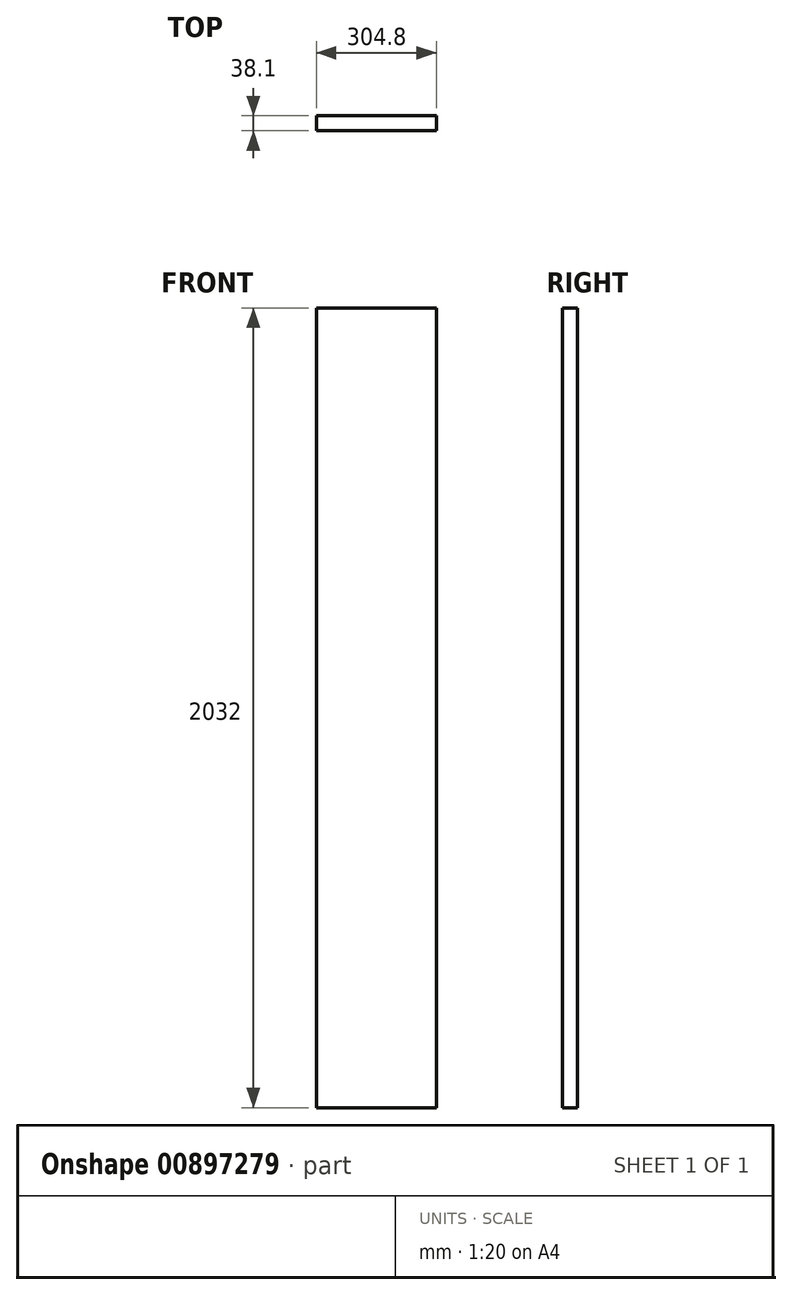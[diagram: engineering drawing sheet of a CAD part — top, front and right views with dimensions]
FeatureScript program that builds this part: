
annotation { "Feature Type Name" : "Feature", "Feature Type Description" : "" }
export const myFeature = defineFeature(function(context is Context, id is Id, definition is map)
    precondition{}
    {
        {
            var Q0;
            Q0=qCreatedBy(makeId("Front.planeOp"),FACE);
            var sketch = newSketch(context, id + "F0", { "sketchPlane" : qUnion([Q0])});
            skLineSegment(sketch, "E0.bottom", {"start": v(-152.4, 1016) * mm, "end": v(152.4, 1016) * mm});
            skLineSegment(sketch, "E0.top", {"start": v(-152.4, -1016) * mm, "end": v(152.4, -1016) * mm});
            skLineSegment(sketch, "E0.left", {"start": v(-152.4, 1016) * mm, "end": v(-152.4, -1016) * mm});
            skLineSegment(sketch, "E0.right", {"start": v(152.4, 1016) * mm, "end": v(152.4, -1016) * mm});
            skPoint(sketch, "E0.middle", {"position": v(0, 0) * mm});
            skSolve(sketch);
        }
        {
            var Q0;
            Q0=makeQuery(id+"F0.imprint","IMPRINT",FACE,{"disambiguationData":[TD([[makeQuery(id+"F0.imprint","IMPRINT",EDGE,{"derivedFrom":sQuery(id+"F0.wireOp",EDGE,"E0.bottom")}),-1.0]])]});
            extrude(context, id + "F1", {"entities" : qUnion([Q0]), "depth" : 38.1 * mm, "offsetDistance" : 25.4 * mm});
        }
    });
